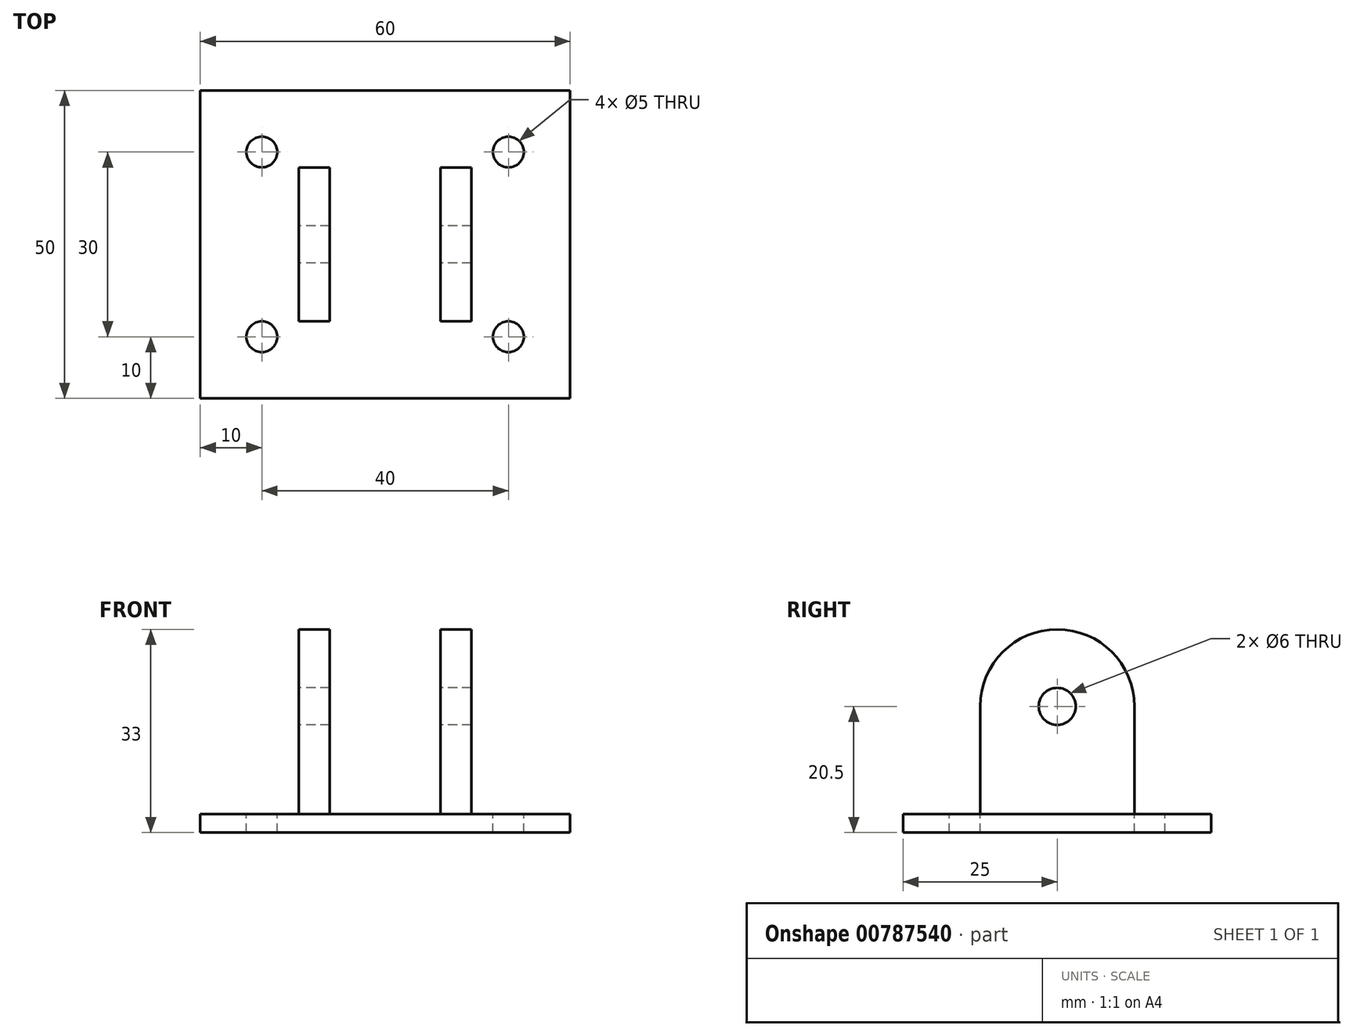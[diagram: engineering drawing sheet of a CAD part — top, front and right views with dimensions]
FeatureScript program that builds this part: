
annotation { "Feature Type Name" : "Feature", "Feature Type Description" : "" }
export const myFeature = defineFeature(function(context is Context, id is Id, definition is map)
    precondition{}
    {
        {
            var Q0;
            Q0=qCreatedBy(makeId("Top.planeOp"),FACE);
            var sketch = newSketch(context, id + "F0", { "sketchPlane" : qUnion([Q0])});
            skLineSegment(sketch, "E0.bottom", {"start": v(-30, 25) * mm, "end": v(30, 25) * mm});
            skLineSegment(sketch, "E0.top", {"start": v(-30, -25) * mm, "end": v(30, -25) * mm});
            skLineSegment(sketch, "E0.left", {"start": v(-30, 25) * mm, "end": v(-30, -25) * mm});
            skLineSegment(sketch, "E0.right", {"start": v(30, 25) * mm, "end": v(30, -25) * mm});
            skSolve(sketch);
        }
        {
            var Q0;
            Q0=makeQuery(id+"F0.imprint","IMPRINT",FACE,{"disambiguationData":[TD([[makeQuery(id+"F0.imprint","IMPRINT",EDGE,{"derivedFrom":sQuery(id+"F0.wireOp",EDGE,"E0.bottom")}),-1.0]])]});
            extrude(context, id + "F1", {"entities" : qUnion([Q0]), "depth" : 3 * mm, "offsetDistance" : 25 * mm});
        }
        {
            var Q0;
            Q0=makeQuery(id+"F1.opExtrude","CAP_FACE",FACE,{"disambiguationData":[OSD([sQuery(id+"F0.wireOp",EDGE,"E0.bottom"),sQuery(id+"F0.wireOp",EDGE,"E0.top"),sQuery(id+"F0.wireOp",EDGE,"E0.left"),sQuery(id+"F0.wireOp",EDGE,"E0.right")])],"isStart":false});
            var sketch = newSketch(context, id + "F2", { "sketchPlane" : qUnion([Q0])});
            skLineSegment(sketch, "E1.bottom", {"start": v(-14, 12.5) * mm, "end": v(-9, 12.5) * mm});
            skLineSegment(sketch, "E1.top", {"start": v(-14, -12.5) * mm, "end": v(-9, -12.5) * mm});
            skLineSegment(sketch, "E1.left", {"start": v(-14, 12.5) * mm, "end": v(-14, -12.5) * mm});
            skLineSegment(sketch, "E1.right", {"start": v(-9, 12.5) * mm, "end": v(-9, -12.5) * mm});
            skLineSegment(sketch, "E2.bottom", {"start": v(9, 12.5) * mm, "end": v(14, 12.5) * mm});
            skLineSegment(sketch, "E2.top", {"start": v(9, -12.5) * mm, "end": v(14, -12.5) * mm});
            skLineSegment(sketch, "E2.left", {"start": v(9, 12.5) * mm, "end": v(9, -12.5) * mm});
            skLineSegment(sketch, "E2.right", {"start": v(14, 12.5) * mm, "end": v(14, -12.5) * mm});
            skSolve(sketch);
        }
        {
            var Q0;
            Q0=makeQuery(id+"F2.imprint","IMPRINT",FACE,{"disambiguationData":[TD([[makeQuery(id+"F2.imprint","IMPRINT",EDGE,{"derivedFrom":sQuery(id+"F2.wireOp",EDGE,"E1.bottom")}),-1.0]])]});
            var Q1;
            Q1=makeQuery(id+"F2.imprint","IMPRINT",FACE,{"disambiguationData":[TD([[makeQuery(id+"F2.imprint","IMPRINT",EDGE,{"derivedFrom":sQuery(id+"F2.wireOp",EDGE,"E2.bottom")}),-1.0]])]});
            extrude(context, id + "F3", {"entities" : qUnion([Q0, Q1]), "operationType" : NewBodyOperationType.ADD, "depth" : 30 * mm, "offsetDistance" : 25 * mm});
        }
        {
            var Q0;
            Q0=makeQuery(id+"F3.opExtrude","CAP_EDGE",EDGE,{"disambiguationData":[OSD([sQuery(id+"F2.wireOp",EDGE,"E1.top")])],"isStart":false});
            var Q1;
            Q1=makeQuery(id+"F3.opExtrude","CAP_EDGE",EDGE,{"disambiguationData":[OSD([sQuery(id+"F2.wireOp",EDGE,"E1.bottom")])],"isStart":false});
            var Q2;
            Q2=makeQuery(id+"F3.opExtrude","CAP_EDGE",EDGE,{"disambiguationData":[OSD([sQuery(id+"F2.wireOp",EDGE,"E2.bottom")])],"isStart":false});
            var Q3;
            Q3=makeQuery(id+"F3.opExtrude","CAP_EDGE",EDGE,{"disambiguationData":[OSD([sQuery(id+"F2.wireOp",EDGE,"E2.top")])],"isStart":false});
            fillet(context, id + "F4", {"entities" : qUnion([Q0, Q1, Q2, Q3]), "radius" : 12.5 * mm, "tangentPropagation" : true, "allowEdgeOverflow" : false});
        }
        {
            var Q0;
            Q0=makeQuery(id+"F3.opExtrude","SWEPT_FACE",FACE,{"disambiguationData":[OSD([sQuery(id+"F2.wireOp",EDGE,"E1.left")])]});
            var sketch = newSketch(context, id + "F5", { "sketchPlane" : qUnion([Q0])});
            skCircle(sketch, "E3", {"center": v(0, 20.5) * mm, "radius": 3 * mm});
            skSolve(sketch);
        }
        {
            var Q0;
            Q0=makeQuery(id+"F5.imprint","IMPRINT",FACE,{"disambiguationData":[TD([[makeQuery(id+"F5.imprint","IMPRINT",EDGE,{"derivedFrom":sQuery(id+"F5.wireOp",EDGE,"E3")}),1.0]])]});
            extrude(context, id + "F6", {"entities" : qUnion([Q0]), "operationType" : NewBodyOperationType.REMOVE, "oppositeDirection" : true, "depth" : 50 * mm, "offsetDistance" : 25 * mm});
        }
        {
            var Q0;
            Q0=makeQuery(id+"F1.opExtrude","CAP_FACE",FACE,{"disambiguationData":[OSD([sQuery(id+"F0.wireOp",EDGE,"E0.bottom"),sQuery(id+"F0.wireOp",EDGE,"E0.top"),sQuery(id+"F0.wireOp",EDGE,"E0.left"),sQuery(id+"F0.wireOp",EDGE,"E0.right")])],"isStart":false});
            var sketch = newSketch(context, id + "F7", { "sketchPlane" : qUnion([Q0])});
            skCircle(sketch, "E4", {"center": v(-20, 15) * mm, "radius": 2.5 * mm});
            skCircle(sketch, "E5", {"center": v(20, 15) * mm, "radius": 2.5 * mm});
            skCircle(sketch, "E6", {"center": v(20, -15) * mm, "radius": 2.5 * mm});
            skCircle(sketch, "E7", {"center": v(-20, -15) * mm, "radius": 2.5 * mm});
            skSolve(sketch);
        }
        {
            var Q0;
            Q0=makeQuery(id+"F7.imprint","IMPRINT",FACE,{"disambiguationData":[TD([[makeQuery(id+"F7.imprint","IMPRINT",EDGE,{"derivedFrom":sQuery(id+"F7.wireOp",EDGE,"E7")}),1.0]])]});
            var Q1;
            Q1=makeQuery(id+"F7.imprint","IMPRINT",FACE,{"disambiguationData":[TD([[makeQuery(id+"F7.imprint","IMPRINT",EDGE,{"derivedFrom":sQuery(id+"F7.wireOp",EDGE,"E4")}),1.0]])]});
            var Q2;
            Q2=makeQuery(id+"F7.imprint","IMPRINT",FACE,{"disambiguationData":[TD([[makeQuery(id+"F7.imprint","IMPRINT",EDGE,{"derivedFrom":sQuery(id+"F7.wireOp",EDGE,"E5")}),1.0]])]});
            var Q3;
            Q3=makeQuery(id+"F7.imprint","IMPRINT",FACE,{"disambiguationData":[TD([[makeQuery(id+"F7.imprint","IMPRINT",EDGE,{"derivedFrom":sQuery(id+"F7.wireOp",EDGE,"E6")}),1.0]])]});
            extrude(context, id + "F8", {"entities" : qUnion([Q0, Q1, Q2, Q3]), "operationType" : NewBodyOperationType.REMOVE, "oppositeDirection" : true, "depth" : 25 * mm, "offsetDistance" : 25 * mm});
        }
    });
